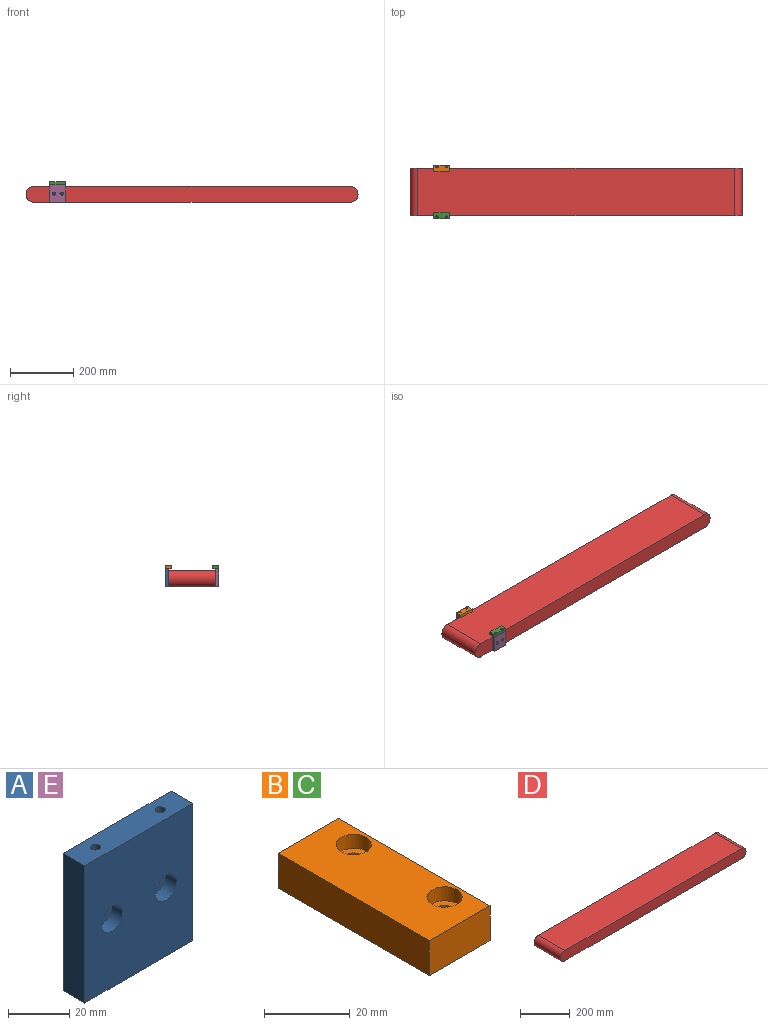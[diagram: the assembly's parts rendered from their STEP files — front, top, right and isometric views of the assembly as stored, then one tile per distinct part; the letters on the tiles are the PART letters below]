
ASSEMBLY  parts=5 mates=4
PART A: 16 faces, bbox 50x10x55 mm
  f0: plane 55x10mm, normal (1,0,0), area 550mm2, adj f1,f3,f4,f5
  f1: plane 50x10mm, normal (0,0,1), area 482.9mm2, adj f0,f2,f4,f5,f13,f15
  f2: plane 55x10mm, normal (-1,0,0), area 550mm2, adj f1,f3,f4,f5
  f3: plane 50x10mm, normal (0,0,-1), area 500mm2, adj f0,f2,f4,f5
  f4: plane 55x50mm, normal (0,-1,0), area 2592.9mm2, adj f0,f1,f2,f3,f8,f11
  f5: plane 55x50mm, normal (0,1,0), area 2710.7mm2, adj f0,f1,f2,f3,f6,f9
  f6: cylinder r=2.5mm len=5mm, axis (0,-1,0), area 78.5mm2, adj f5,f7
  f7: plane 10x10mm, normal (0,-1,0), area 58.9mm2, adj f6,f8
  f8: cylinder r=5mm len=10mm, axis (0,-1,0), area 157.1mm2, adj f4,f7
  f9: cylinder r=2.5mm len=5mm, axis (0,-1,0), area 78.5mm2, adj f5,f10
  f10: plane 10x10mm, normal (0,-1,0), area 58.9mm2, adj f9,f11
  f11: cylinder r=5mm len=10mm, axis (0,-1,0), area 157.1mm2, adj f4,f10
  f12: cone r=0mm half-angle=59deg, axis (0,0,1), area 10mm2, adj f13
  f13: cylinder r=1.65mm len=14.1mm, axis (0,0,1), area 146.2mm2, adj f1,f12
  f14: cone r=0mm half-angle=59deg, axis (0,0,1), area 10mm2, adj f15
  f15: cylinder r=1.65mm len=14.1mm, axis (0,0,1), area 146.2mm2, adj f1,f14
PART B: 12 faces, bbox 20x50x10 mm
  f0: plane 20x10mm, normal (0,-1,0), area 200mm2, adj f1,f3,f4,f5
  f1: plane 50x10mm, normal (1,0,0), area 500mm2, adj f0,f2,f4,f5
  f2: plane 20x10mm, normal (0,1,0), area 200mm2, adj f1,f3,f4,f5
  f3: plane 50x10mm, normal (-1,0,0), area 500mm2, adj f0,f2,f4,f5
  f4: plane 50x20mm, normal (0,0,1), area 893.1mm2, adj f0,f1,f2,f3,f8,f11
  f5: plane 50x20mm, normal (0,0,-1), area 968.2mm2, adj f0,f1,f2,f3,f6,f9
  f6: cylinder r=2.25mm len=6mm, axis (0,0,1), area 84.8mm2, adj f5,f7
  f7: plane 8.25x8.25mm, normal (0,0,1), area 37.6mm2, adj f6,f8
  f8: cylinder r=4.12mm len=8.25mm, axis (0,0,1), area 103.7mm2, adj f4,f7
  f9: cylinder r=2.25mm len=6mm, axis (0,0,1), area 84.8mm2, adj f5,f10
  f10: plane 8.25x8.25mm, normal (0,0,1), area 37.6mm2, adj f9,f11
  f11: cylinder r=4.12mm len=8.25mm, axis (0,0,1), area 103.7mm2, adj f4,f10
PART C: same geometry as B
PART D: 6 faces, bbox 1050x150x50 mm
  f0: plane 1000x150mm, normal (0,0,-1), area 150000mm2, adj f1,f3,f4,f5
  f1: cylinder r=25mm len=150mm, axis (0,1,0), area 11781mm2, adj f0,f2,f4,f5
  f2: plane 1000x150mm, normal (0,0,1), area 150000mm2, adj f1,f3,f4,f5
  f3: cylinder r=25mm len=150mm, axis (0,1,0), area 11781mm2, adj f0,f2,f4,f5
  f4: plane 1050x50mm, normal (0,-1,0), area 51963.5mm2, adj f0,f1,f2,f3
  f5: plane 1050x50mm, normal (0,1,0), area 51963.5mm2, adj f0,f1,f2,f3
PART E: same geometry as A
PLACE A rot(axis=(0,0,1),180deg) t=(-425,75,2.5)mm
PLACE B rot(axis=(0,0,1),90deg) t=(-425,75,30)mm
PLACE C rot(axis=(0,0,-1),90deg) t=(-425,-75,30)mm
PLACE D at identity fixed
PLACE E t=(-425,-75,2.5)mm
MATE fastened A.f5 <-> D.f5  axis (0,-1,0) through (-450,75,-25)mm
MATE fastened C.f6 <-> E.f14  axis (0,0,1) through (-440,-80,30)mm
MATE fastened D.f4 <-> E.f5  axis (0,-1,0) through (-500,-75,-25)mm
MATE fastened B.f6 <-> A.f14  axis (0,0,-1) through (-410,80,30)mm
